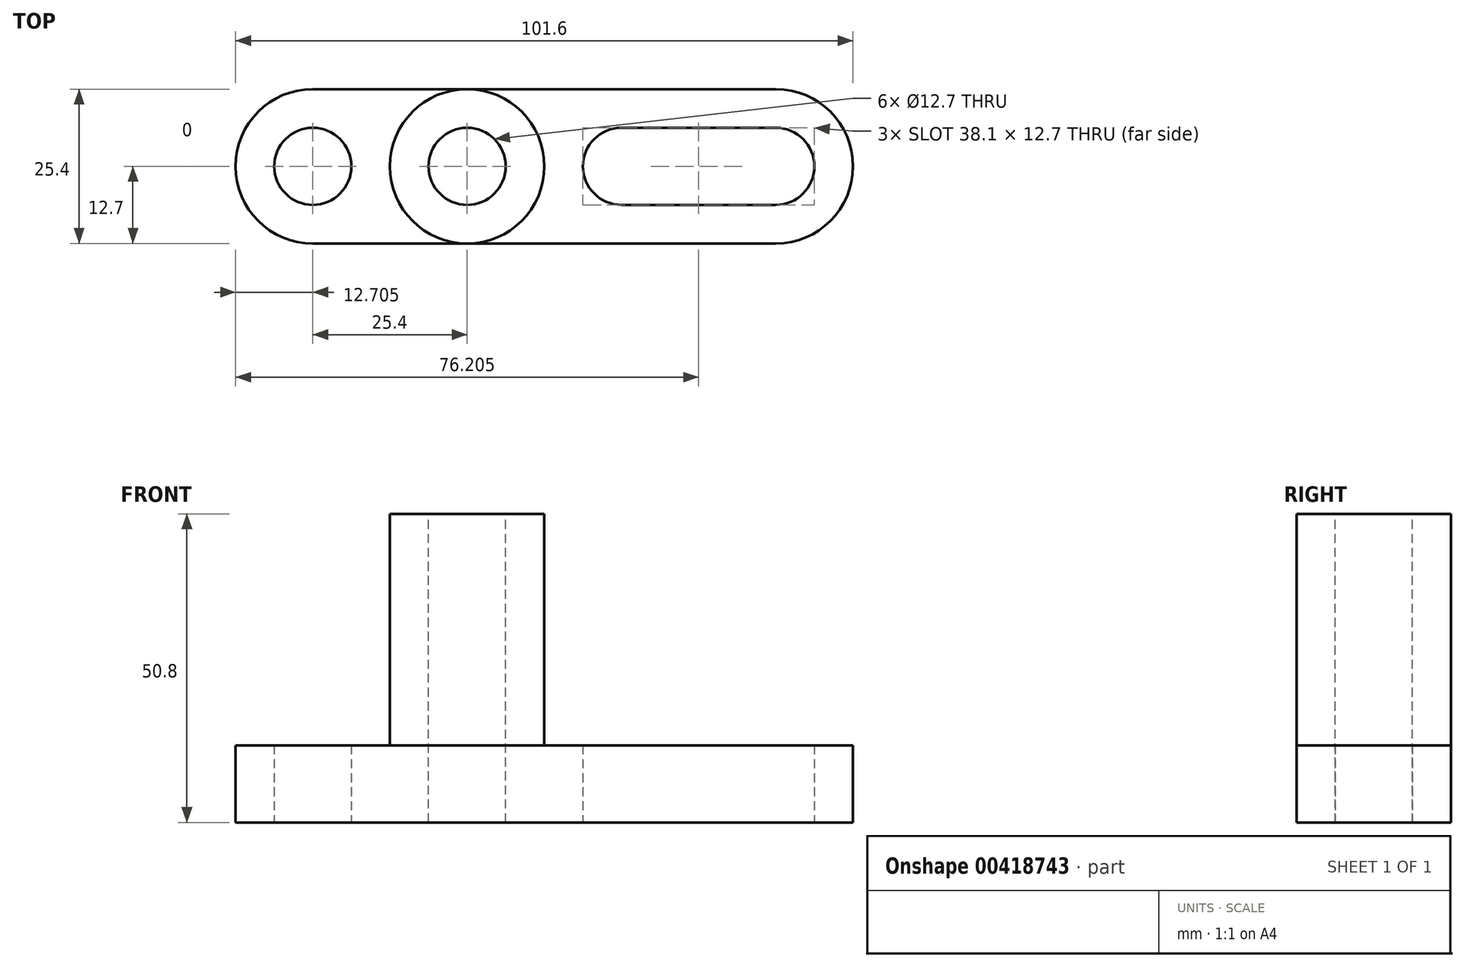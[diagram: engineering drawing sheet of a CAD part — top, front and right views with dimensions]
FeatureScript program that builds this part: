
annotation { "Feature Type Name" : "Feature", "Feature Type Description" : "" }
export const myFeature = defineFeature(function(context is Context, id is Id, definition is map)
    precondition{}
    {
        {
            var Q0;
            Q0=qCreatedBy(makeId("Front.planeOp"),FACE);
            var sketch = newSketch(context, id + "F0", { "sketchPlane" : qUnion([Q0])});
            skLineSegment(sketch, "E0.bottom", {"start": v(26.7, 0) * mm, "end": v(-74.9, 0) * mm});
            skLineSegment(sketch, "E0.top", {"start": v(26.7, 50.8) * mm, "end": v(-74.9, 50.8) * mm});
            skLineSegment(sketch, "E0.left", {"start": v(26.7, 0) * mm, "end": v(26.7, 50.8) * mm});
            skLineSegment(sketch, "E0.right", {"start": v(-74.9, 0) * mm, "end": v(-74.9, 50.8) * mm});
            skSolve(sketch);
        }
        {
            var Q0;
            Q0=makeQuery(id+"F0.imprint","IMPRINT",FACE,{"disambiguationData":[TD([[makeQuery(id+"F0.imprint","IMPRINT",EDGE,{"derivedFrom":sQuery(id+"F0.wireOp",EDGE,"E0.bottom")}),-1.0]])]});
            extrude(context, id + "F1", {"entities" : qUnion([Q0]), "depth" : 25.4 * mm});
        }
        {
            var Q0;
            Q0=makeQuery(id+"F1.opExtrude","CAP_FACE",FACE,{"disambiguationData":[OSD([sQuery(id+"F0.wireOp",EDGE,"E0.bottom"),sQuery(id+"F0.wireOp",EDGE,"E0.top"),sQuery(id+"F0.wireOp",EDGE,"E0.left"),sQuery(id+"F0.wireOp",EDGE,"E0.right")])],"isStart":false});
            var sketch = newSketch(context, id + "F2", { "sketchPlane" : qUnion([Q0])});
            skLineSegment(sketch, "E1.bottom", {"start": v(-24.1, 50.8) * mm, "end": v(26.7, 50.8) * mm});
            skLineSegment(sketch, "E1.top", {"start": v(-24.1, 12.7) * mm, "end": v(26.7, 12.7) * mm});
            skLineSegment(sketch, "E1.left", {"start": v(-24.1, 50.8) * mm, "end": v(-24.1, 12.7) * mm});
            skLineSegment(sketch, "E1.right", {"start": v(26.7, 50.8) * mm, "end": v(26.7, 12.7) * mm});
            skSolve(sketch);
        }
        {
            var Q0;
            Q0=makeQuery(id+"F2.imprint","IMPRINT",FACE,{"disambiguationData":[TD([[makeQuery(id+"F2.imprint","IMPRINT",EDGE,{"derivedFrom":sQuery(id+"F2.wireOp",EDGE,"E1.bottom")}),1.0]])]});
            extrude(context, id + "F3", {"entities" : qUnion([Q0]), "operationType" : NewBodyOperationType.REMOVE, "oppositeDirection" : true, "depth" : 25.4 * mm});
        }
        {
            var Q0;
            Q0=makeQuery(id+"F1.opExtrude","SWEPT_FACE",FACE,{"disambiguationData":[OSD([sQuery(id+"F0.wireOp",EDGE,"E0.top")])]});
            var sketch = newSketch(context, id + "F4", { "sketchPlane" : qUnion([Q0])});
            skCircle(sketch, "E2", {"center": v(-36.8, -12.7) * mm, "radius": 12.7 * mm});
            skLineSegment(sketch, "E3", {"start": v(-49.5, 0) * mm, "end": v(-49.5, -25.4) * mm});
            skLineSegment(sketch, "E4", {"start": v(-49.5, -25.4) * mm, "end": v(-74.9, -25.4) * mm});
            skLineSegment(sketch, "E5", {"start": v(-74.9, -25.4) * mm, "end": v(-74.9, 0) * mm});
            skLineSegment(sketch, "E6", {"start": v(-74.9, 0) * mm, "end": v(-49.5, 0) * mm});
            skLineSegment(sketch, "E7", {"start": v(-49.5, 0) * mm, "end": v(-24.1, 0) * mm});
            skLineSegment(sketch, "E8", {"start": v(-24.1, 0) * mm, "end": v(-24.1, -25.4) * mm});
            skLineSegment(sketch, "E9", {"start": v(-24.1, -25.4) * mm, "end": v(-49.5, -25.4) * mm});
            skSolve(sketch);
        }
        {
            var Q0;
            {var subQ0=sQuery(id+"F4.wireOp",EDGE,"E4");Q0=makeQuery(id+"F4.imprint","IMPRINT",FACE,{"disambiguationData":[TD([[makeQuery(id+"F4.imprint","IMPRINT",EDGE,{"derivedFrom":subQ0}),-1.0]])]});}
            var Q1;
            {var subQ0=sQuery(id+"F4.wireOp",EDGE,"E8");var subQ1=sQuery(id+"F4.wireOp",EDGE,"E2");var subQ2=makeQuery(id+"F4.imprint","INTERSECT",VERTEX,{"derivedFrom":[subQ1,subQ0]});Q1=makeQuery(id+"F4.imprint","IMPRINT",FACE,{"disambiguationData":[TD([[makeQuery(id+"F4.imprint","IMPRINT",EDGE,{"disambiguationData":[TD([[subQ2,1.0]])],"derivedFrom":subQ1}),-1.0]])]});}
            var Q2;
            {var subQ0=sQuery(id+"F4.wireOp",EDGE,"E7");var subQ1=sQuery(id+"F4.wireOp",EDGE,"E2");var subQ2=makeQuery(id+"F4.imprint","INTERSECT",VERTEX,{"derivedFrom":[subQ1,subQ0]});Q2=makeQuery(id+"F4.imprint","IMPRINT",FACE,{"disambiguationData":[TD([[makeQuery(id+"F4.imprint","IMPRINT",EDGE,{"disambiguationData":[TD([[subQ2,1.0]])],"derivedFrom":subQ1}),-1.0]])]});}
            var Q3;
            {var subQ0=sQuery(id+"F4.wireOp",EDGE,"E9");var subQ1=sQuery(id+"F4.wireOp",EDGE,"E2");var subQ2=makeQuery(id+"F4.imprint","INTERSECT",VERTEX,{"derivedFrom":[subQ1,subQ0]});Q3=makeQuery(id+"F4.imprint","IMPRINT",FACE,{"disambiguationData":[TD([[makeQuery(id+"F4.imprint","IMPRINT",EDGE,{"disambiguationData":[TD([[subQ2,1.0]])],"derivedFrom":subQ1}),-1.0]])]});}
            var Q4;
            {var subQ0=sQuery(id+"F4.wireOp",EDGE,"E7");var subQ1=sQuery(id+"F4.wireOp",EDGE,"E2");var subQ2=makeQuery(id+"F4.imprint","INTERSECT",VERTEX,{"derivedFrom":[subQ1,subQ0]});Q4=makeQuery(id+"F4.imprint","IMPRINT",FACE,{"disambiguationData":[TD([[makeQuery(id+"F4.imprint","IMPRINT",EDGE,{"disambiguationData":[TD([[subQ2,-1.0]])],"derivedFrom":subQ1}),-1.0]])]});}
            extrude(context, id + "F5", {"entities" : qUnion([Q0, Q1, Q2, Q3, Q4]), "operationType" : NewBodyOperationType.REMOVE, "oppositeDirection" : true, "depth" : 38.1 * mm});
        }
        {
            var Q0;
            Q0=makeQuery(id+"F1.opExtrude","SWEPT_FACE",FACE,{"disambiguationData":[OSD([sQuery(id+"F0.wireOp",EDGE,"E0.top")])]});
            var sketch = newSketch(context, id + "F6", { "sketchPlane" : qUnion([Q0])});
            skCircle(sketch, "E10", {"center": v(-36.8, -12.7) * mm, "radius": 6.35 * mm});
            skSolve(sketch);
        }
        {
            var Q0;
            Q0=makeQuery(id+"F6.imprint","IMPRINT",FACE,{"disambiguationData":[TD([[makeQuery(id+"F6.imprint","IMPRINT",EDGE,{"derivedFrom":sQuery(id+"F6.wireOp",EDGE,"E10")}),1.0]])]});
            extrude(context, id + "F7", {"entities" : qUnion([Q0]), "operationType" : NewBodyOperationType.REMOVE, "oppositeDirection" : true, "depth" : 50.8 * mm});
        }
        {
            var Q0;
            Q0=qCreatedBy(makeId("Top.planeOp"),FACE);
            var sketch = newSketch(context, id + "F8", { "sketchPlane" : qUnion([Q0])});
            skCircle(sketch, "E11", {"center": v(-62.2, -12.7) * mm, "radius": 6.35 * mm});
            skCircle(sketch, "E12", {"center": v(-11.4, -12.7) * mm, "radius": 6.35 * mm});
            skCircle(sketch, "E13", {"center": v(14, -12.7) * mm, "radius": 6.35 * mm});
            skLineSegment(sketch, "E14", {"start": v(14, -6.35) * mm, "end": v(-11.4, -6.35) * mm});
            skLineSegment(sketch, "E15", {"start": v(-11.4, -6.35) * mm, "end": v(14, -6.35) * mm});
            skLineSegment(sketch, "E16", {"start": v(14, -19.05) * mm, "end": v(-11.4, -19.05) * mm});
            skLineSegment(sketch, "E17", {"start": v(-11.4, -19.05) * mm, "end": v(14, -19.05) * mm});
            skArc(sketch, "E18", {"start": v(-74.9, -12.7) * mm, "mid": v(-71.18, -21.68) * mm, "end": v(-62.2, -25.4) * mm});
            skArc(sketch, "E19", {"start": v(-62.2, 0) * mm, "mid": v(-71.18, -3.72) * mm, "end": v(-74.9, -12.7) * mm});
            skLineSegment(sketch, "E20", {"start": v(-62.2, -25.4) * mm, "end": v(-74.9, -25.4) * mm});
            skLineSegment(sketch, "E21", {"start": v(-74.9, -25.4) * mm, "end": v(-74.9, -12.7) * mm});
            skLineSegment(sketch, "E22", {"start": v(-74.9, -12.7) * mm, "end": v(-74.9, 0) * mm});
            skLineSegment(sketch, "E23", {"start": v(-74.9, 0) * mm, "end": v(-62.2, 0) * mm});
            skArc(sketch, "E24", {"start": v(26.7, -12.7) * mm, "mid": v(22.98, -3.72) * mm, "end": v(14, 0) * mm});
            skArc(sketch, "E25", {"start": v(14, -25.4) * mm, "mid": v(22.98, -21.68) * mm, "end": v(26.7, -12.7) * mm});
            skLineSegment(sketch, "E26", {"start": v(26.7, -12.7) * mm, "end": v(26.7, 0) * mm});
            skLineSegment(sketch, "E27", {"start": v(26.7, 0) * mm, "end": v(14, 0) * mm});
            skLineSegment(sketch, "E28", {"start": v(26.7, -12.7) * mm, "end": v(26.7, -25.4) * mm});
            skLineSegment(sketch, "E29", {"start": v(26.7, -25.4) * mm, "end": v(14, -25.4) * mm});
            skSolve(sketch);
        }
        {
            var Q0;
            Q0 = qSketchRegion(id + "F8", true);
            extrude(context, id + "F9", {"entities" : qUnion([Q0]), "operationType" : NewBodyOperationType.REMOVE, "depth" : 25.4 * mm});
        }
    });
